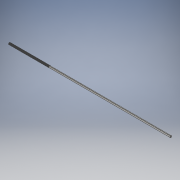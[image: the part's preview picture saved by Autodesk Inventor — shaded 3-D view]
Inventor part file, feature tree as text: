
AUTODESK INVENTOR PART (.ipt)
format: ipt  version: 2019.4 (Build 234330000, 330)  size: 1,553,920 bytes
history: native  units: mm
features: extrude x1, thread x1, sketch x1, mirror x1
ambient origin geometry x8: Origin, YZ Plane, XZ Plane, XY Plane, X Axis, Y Axis, Z Axis, Center Point
bodies: Solid1 (feature_tree)
feature tree (4):
  extrude  "Extrusion1"  Depth=225.0mm TaperAngle=0.0deg
  thread  "Thread1"  [1 undecoded]
  sketch  "Sketch1"  dims[d0=3.65mm d1=225.0mm d2=0.0mm d3=10.0mm d4=0.0mm]
  mirror  "Mirror1"
note: 1 required parameter value undecoded (feature->parameter linkage not recoverable at this tier; creation-order binding heuristic only, values carry confidence <= 0.55)
